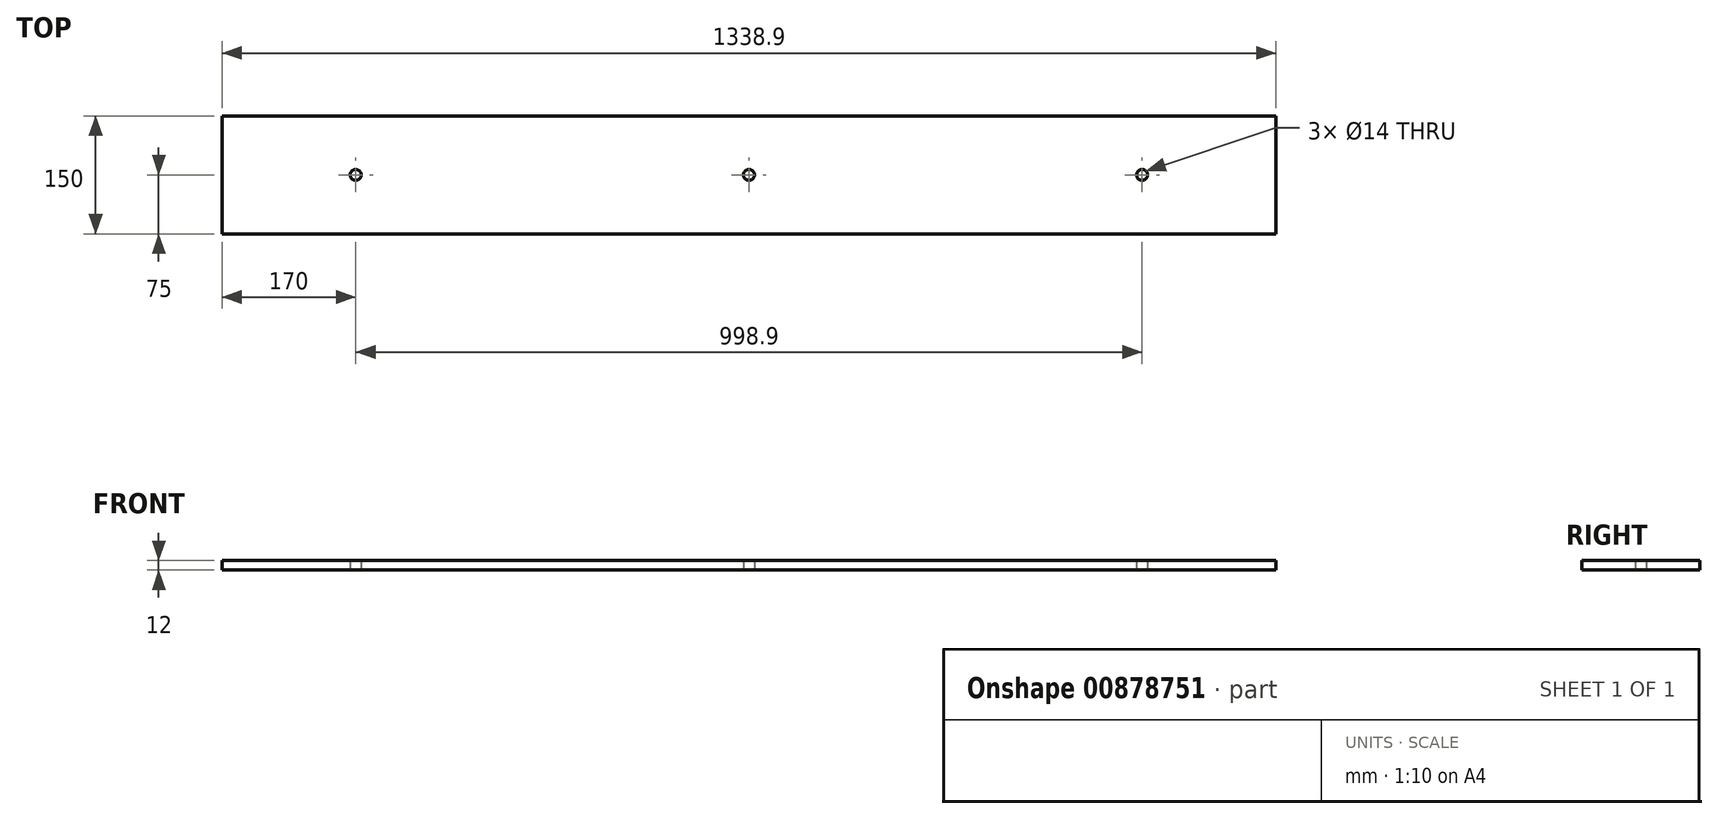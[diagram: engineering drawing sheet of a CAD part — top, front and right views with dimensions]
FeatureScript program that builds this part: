
annotation { "Feature Type Name" : "Feature", "Feature Type Description" : "" }
export const myFeature = defineFeature(function(context is Context, id is Id, definition is map)
    precondition{}
    {
        {
            var Q0;
            Q0=qCreatedBy(makeId("Top.planeOp"),FACE);
            var sketch = newSketch(context, id + "F0", { "sketchPlane" : qUnion([Q0])});
            skLineSegment(sketch, "E0.bottom", {"start": v(669.45, 75) * mm, "end": v(-669.45, 75) * mm});
            skLineSegment(sketch, "E0.top", {"start": v(669.45, -75) * mm, "end": v(-669.45, -75) * mm});
            skLineSegment(sketch, "E0.left", {"start": v(669.45, 75) * mm, "end": v(669.45, -75) * mm});
            skLineSegment(sketch, "E0.right", {"start": v(-669.45, 75) * mm, "end": v(-669.45, -75) * mm});
            skPoint(sketch, "E0.middle", {"position": v(0, 0) * mm});
            skCircle(sketch, "E1", {"center": v(-499.45, 0) * mm, "radius": 7 * mm});
            skCircle(sketch, "E2", {"center": v(0, 0) * mm, "radius": 7 * mm});
            skCircle(sketch, "E3", {"center": v(499.45, 0) * mm, "radius": 7 * mm});
            skSolve(sketch);
        }
        {
            var Q0;
            Q0=makeQuery(id+"F0.imprint","IMPRINT",FACE,{"disambiguationData":[TD([[makeQuery(id+"F0.imprint","IMPRINT",EDGE,{"derivedFrom":sQuery(id+"F0.wireOp",EDGE,"E0.bottom")}),1.0]])]});
            extrude(context, id + "F1", {"entities" : qUnion([Q0]), "depth" : 12 * mm, "offsetDistance" : 25 * mm});
        }
    });
